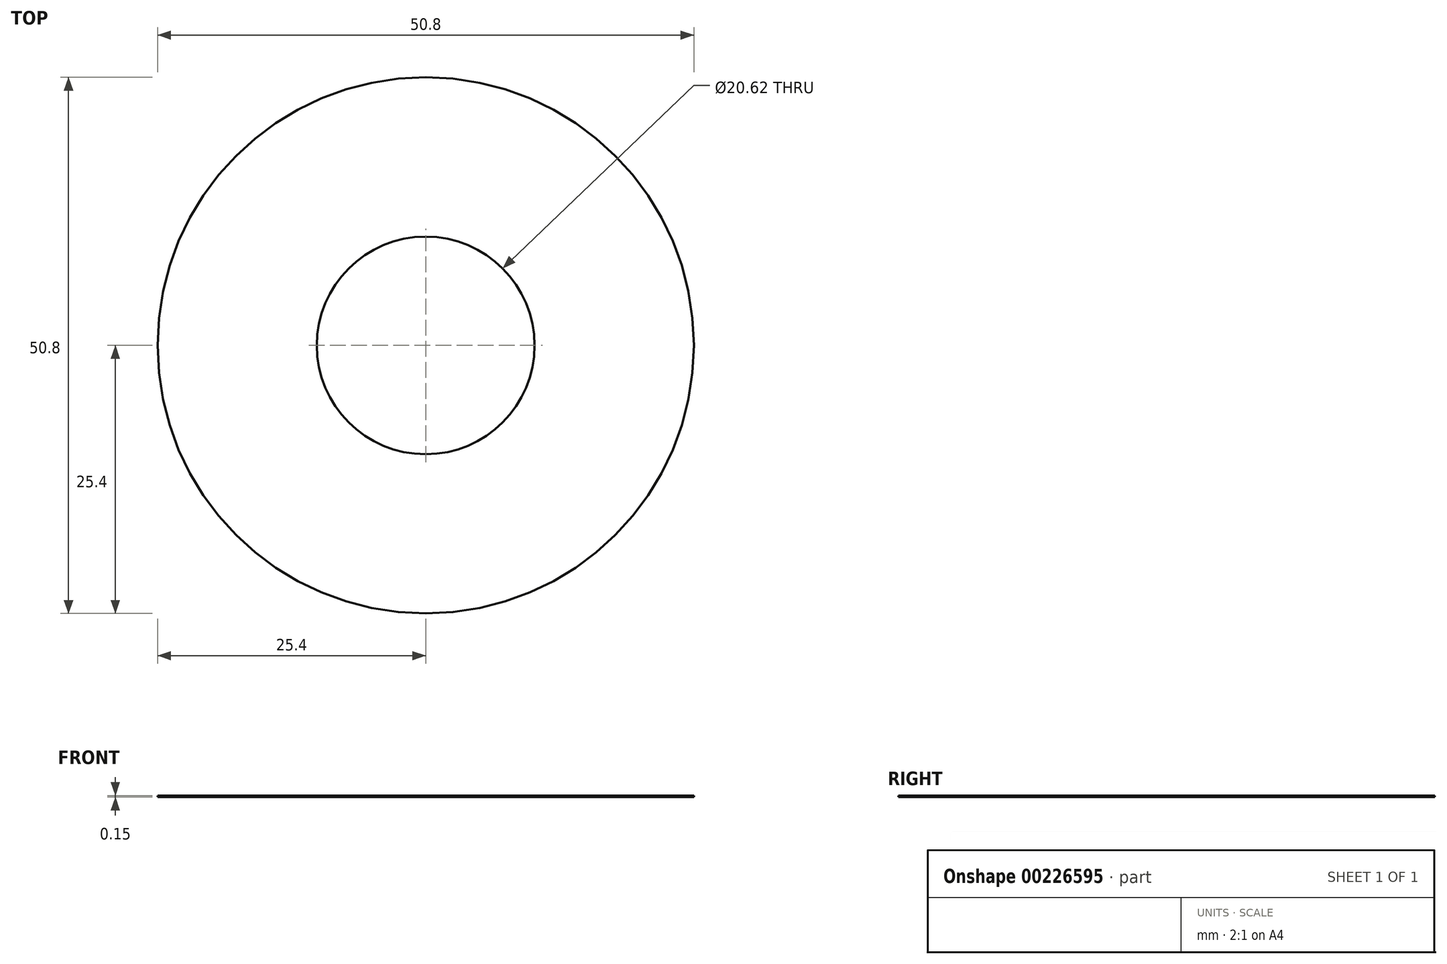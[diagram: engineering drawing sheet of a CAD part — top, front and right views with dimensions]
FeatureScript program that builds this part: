
annotation { "Feature Type Name" : "Feature", "Feature Type Description" : "" }
export const myFeature = defineFeature(function(context is Context, id is Id, definition is map)
    precondition{}
    {
        {
            var Q0;
            Q0=qCreatedBy(makeId("Top.planeOp"),FACE);
            var sketch = newSketch(context, id + "F0", { "sketchPlane" : qUnion([Q0])});
            skCircle(sketch, "E0", {"center": v(0, 0) * mm, "radius": 10.31 * mm});
            skCircle(sketch, "E1", {"center": v(0, 0) * mm, "radius": 25.4 * mm});
            skSolve(sketch);
        }
        {
            var Q0;
            Q0=makeQuery(id+"F0.imprint","IMPRINT",FACE,{"disambiguationData":[TD([[makeQuery(id+"F0.imprint","IMPRINT",EDGE,{"derivedFrom":sQuery(id+"F0.wireOp",EDGE,"E0")}),-1.0]])]});
            extrude(context, id + "F1", {"entities" : qUnion([Q0]), "depth" : ((0.12 + 0.18) / 2) * mm});
        }
    });
